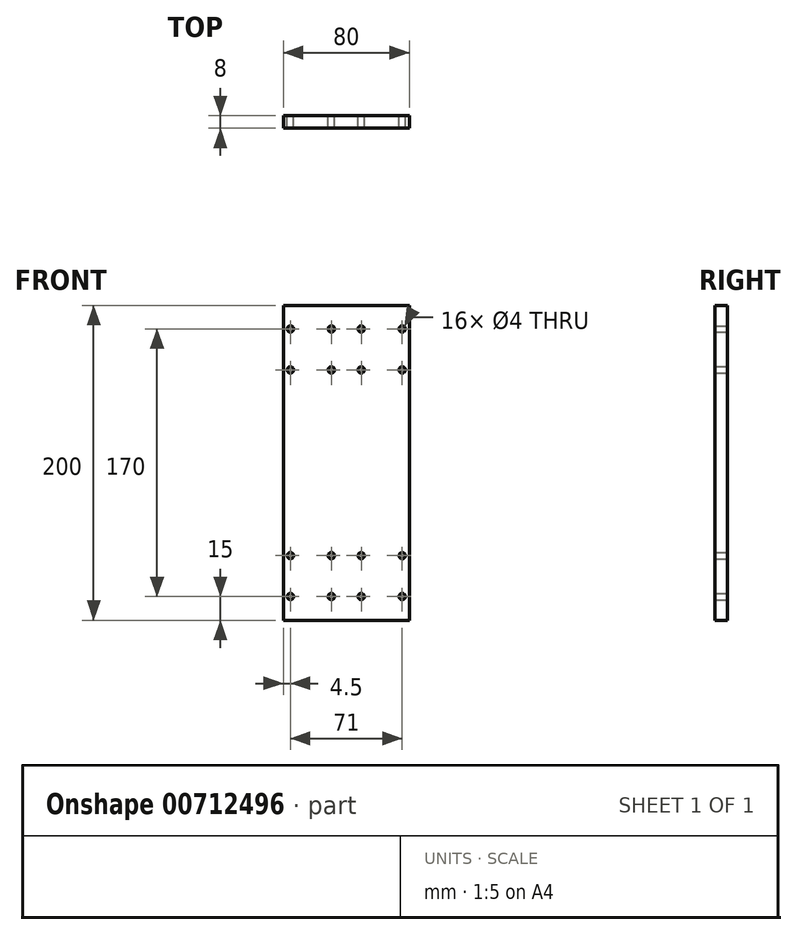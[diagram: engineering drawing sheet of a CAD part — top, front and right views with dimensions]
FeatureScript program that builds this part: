
annotation { "Feature Type Name" : "Feature", "Feature Type Description" : "" }
export const myFeature = defineFeature(function(context is Context, id is Id, definition is map)
    precondition{}
    {
        {
            var Q0;
            Q0=qCreatedBy(makeId("Front.planeOp"),FACE);
            var sketch = newSketch(context, id + "F0", { "sketchPlane" : qUnion([Q0])});
            skLineSegment(sketch, "E0.bottom", {"start": v(40, -100) * mm, "end": v(-40, -100) * mm});
            skLineSegment(sketch, "E0.top", {"start": v(40, 100) * mm, "end": v(-40, 100) * mm});
            skLineSegment(sketch, "E0.left", {"start": v(40, -100) * mm, "end": v(40, 100) * mm});
            skLineSegment(sketch, "E0.right", {"start": v(-40, -100) * mm, "end": v(-40, 100) * mm});
            skPoint(sketch, "E0.middle", {"position": v(0, 0) * mm});
            skCircle(sketch, "E1", {"center": v(-35.5, 85) * mm, "radius": 2 * mm});
            skLineSegment(sketch, "E2", {"start": v(-22.5, 85) * mm, "end": v(-22.5, 59) * mm, "construction": true});
            skCircle(sketch, "E3", {"center": v(-35.5, 59) * mm, "radius": 2 * mm});
            skCircle(sketch, "E4.MirrorC", {"center": v(-9.5, 59) * mm, "radius": 2 * mm});
            skCircle(sketch, "E5.MirrorC", {"center": v(-9.5, 85) * mm, "radius": 2 * mm});
            skCircle(sketch, "E6.MirrorC", {"center": v(35.5, 85) * mm, "radius": 2 * mm});
            skCircle(sketch, "E7.MirrorC", {"center": v(35.5, 59) * mm, "radius": 2 * mm});
            skCircle(sketch, "E8.MirrorC", {"center": v(9.5, 59) * mm, "radius": 2 * mm});
            skCircle(sketch, "E9.MirrorC", {"center": v(9.5, 85) * mm, "radius": 2 * mm});
            skLineSegment(sketch, "E10.MirrorCS", {"start": v(22.5, 85) * mm, "end": v(22.5, 59) * mm, "construction": true});
            skCircle(sketch, "E11.MirrorC", {"center": v(9.5, -85) * mm, "radius": 2 * mm});
            skCircle(sketch, "E12.MirrorC", {"center": v(9.5, -59) * mm, "radius": 2 * mm});
            skCircle(sketch, "E13.MirrorC", {"center": v(35.5, -59) * mm, "radius": 2 * mm});
            skCircle(sketch, "E14.MirrorC", {"center": v(35.5, -85) * mm, "radius": 2 * mm});
            skCircle(sketch, "E15.MirrorC", {"center": v(-9.5, -85) * mm, "radius": 2 * mm});
            skCircle(sketch, "E16.MirrorC", {"center": v(-9.5, -59) * mm, "radius": 2 * mm});
            skCircle(sketch, "E17.MirrorC", {"center": v(-35.5, -59) * mm, "radius": 2 * mm});
            skCircle(sketch, "E18.MirrorC", {"center": v(-35.5, -85) * mm, "radius": 2 * mm});
            skLineSegment(sketch, "E19.MirrorCS", {"start": v(22.5, -85) * mm, "end": v(22.5, -59) * mm, "construction": true});
            skLineSegment(sketch, "E20.MirrorCS", {"start": v(-22.5, -85) * mm, "end": v(-22.5, -59) * mm, "construction": true});
            skSolve(sketch);
        }
        {
            var Q0;
            Q0 = qSketchRegion(id + "F0", true);
            extrude(context, id + "F1", {"entities" : qUnion([Q0]), "depth" : 8 * mm, "offsetDistance" : 25 * mm});
        }
    });
